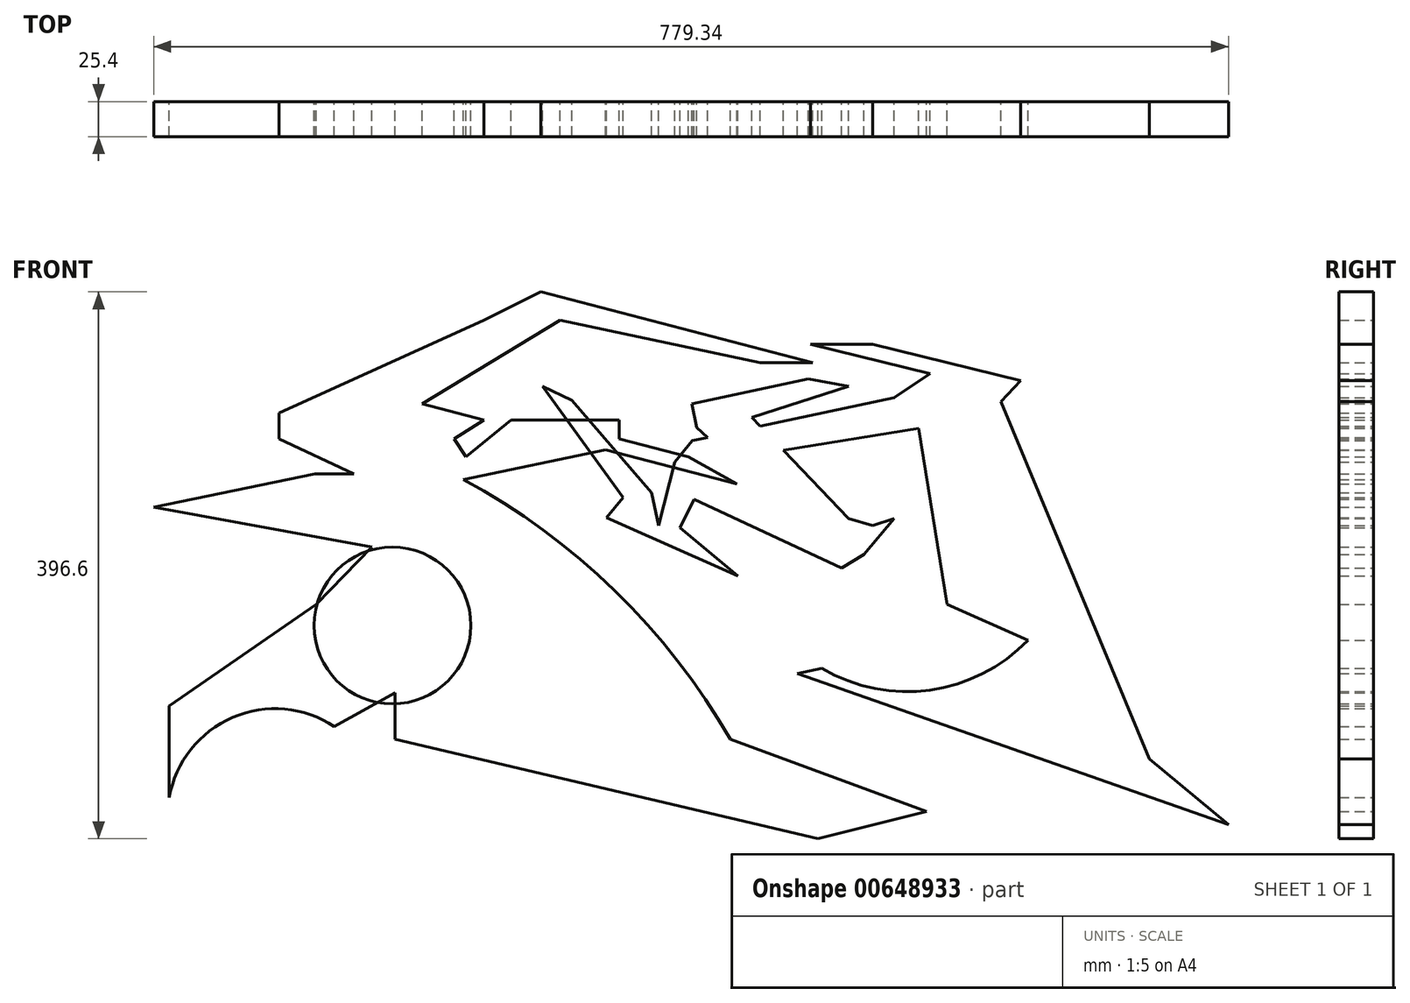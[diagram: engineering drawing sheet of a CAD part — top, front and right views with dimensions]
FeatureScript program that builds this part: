
annotation { "Feature Type Name" : "Feature", "Feature Type Description" : "" }
export const myFeature = defineFeature(function(context is Context, id is Id, definition is map)
    precondition{}
    {
        {
            var Q0;
            Q0=qCreatedBy(makeId("Front.planeOp"),FACE);
            var sketch = newSketch(context, id + "F0", { "sketchPlane" : qUnion([Q0])});
            skCircle(sketch, "E0", {"center": v(-11.54, -15.47) * mm, "radius": 56.87 * mm});
            skLineSegment(sketch, "E1", {"start": v(-55.28, -53.52) * mm, "end": v(-83.75, -13.85) * mm});
            skLineSegment(sketch, "E2", {"start": v(-83.75, -13.85) * mm, "end": v(-75.93, -41.97) * mm});
            skSolve(sketch);
        }
        {
            var Q0;
            Q0=qCreatedBy(makeId("Front.planeOp"),FACE);
            var sketch = newSketch(context, id + "F1", { "sketchPlane" : qUnion([Q0])});
            skLineSegment(sketch, "E3", {"start": v(97.36, 93.18) * mm, "end": v(97.36, 103.13) * mm});
            skLineSegment(sketch, "E4", {"start": v(97.36, 103.13) * mm, "end": v(130.3, 111.83) * mm});
            skLineSegment(sketch, "E5", {"start": v(130.3, 111.83) * mm, "end": v(314.3, 26.05) * mm});
            skLineSegment(sketch, "E6", {"start": v(314.3, 26.05) * mm, "end": v(330.46, 36) * mm});
            skLineSegment(sketch, "E7", {"start": v(330.46, 36) * mm, "end": v(352.21, 62.1) * mm});
            skLineSegment(sketch, "E8", {"start": v(352.21, 62.1) * mm, "end": v(336.67, 57.13) * mm});
            skLineSegment(sketch, "E9", {"start": v(336.67, 57.13) * mm, "end": v(319.27, 62.1) * mm});
            skLineSegment(sketch, "E10", {"start": v(319.27, 62.1) * mm, "end": v(249.03, 135.45) * mm});
            skLineSegment(sketch, "E11", {"start": v(249.03, 135.45) * mm, "end": v(319.27, 157.83) * mm});
            skLineSegment(sketch, "E12", {"start": v(319.27, 157.83) * mm, "end": v(290.06, 163.42) * mm});
            skLineSegment(sketch, "E13", {"start": v(290.06, 163.42) * mm, "end": v(205.52, 145.4) * mm});
            skLineSegment(sketch, "E14", {"start": v(205.52, 145.4) * mm, "end": v(209.2, 128.15) * mm});
            skLineSegment(sketch, "E15", {"start": v(209.2, 128.15) * mm, "end": v(300, 42.21) * mm});
            skLineSegment(sketch, "E16", {"start": v(130.3, 234.42) * mm, "end": v(115.42, 202.5) * mm});
            skLineSegment(sketch, "E17", {"start": v(115.42, 202.5) * mm, "end": v(118.58, 202.5) * mm});
            skLineSegment(sketch, "E18", {"start": v(97.36, 157.83) * mm, "end": v(118.58, 147.93) * mm});
            skLineSegment(sketch, "E19", {"start": v(118.58, 147.93) * mm, "end": v(176.52, 80.93) * mm});
            skLineSegment(sketch, "E20", {"start": v(176.52, 80.93) * mm, "end": v(181.6, 57.13) * mm});
            skLineSegment(sketch, "E21", {"start": v(181.6, 57.13) * mm, "end": v(193.17, 103.13) * mm});
            skLineSegment(sketch, "E22", {"start": v(193.17, 103.13) * mm, "end": v(206.05, 118.58) * mm});
            skLineSegment(sketch, "E23", {"start": v(206.05, 118.58) * mm, "end": v(352.21, 149.74) * mm});
            skLineSegment(sketch, "E24", {"start": v(352.21, 149.74) * mm, "end": v(378.29, 167.06) * mm});
            skLineSegment(sketch, "E25", {"start": v(378.29, 167.06) * mm, "end": v(291.68, 188.47) * mm});
            skLineSegment(sketch, "E26", {"start": v(291.68, 188.47) * mm, "end": v(336.67, 188.47) * mm});
            skLineSegment(sketch, "E27", {"start": v(336.67, 188.47) * mm, "end": v(443.94, 161.95) * mm});
            skLineSegment(sketch, "E28", {"start": v(443.94, 161.95) * mm, "end": v(429.7, 146.92) * mm});
            skLineSegment(sketch, "E29", {"start": v(429.7, 146.92) * mm, "end": v(537.48, -112.1) * mm});
            skLineSegment(sketch, "E30", {"start": v(537.48, -112.1) * mm, "end": v(594.7, -159.8) * mm});
            skLineSegment(sketch, "E31", {"start": v(594.7, -159.8) * mm, "end": v(282.12, -50.37) * mm});
            skLineSegment(sketch, "E32", {"start": v(282.12, -50.37) * mm, "end": v(300, -46.56) * mm});
            skArc(sketch, "E33", {"start": v(300, -46.56) * mm, "mid": v(378.34, -62.26) * mm, "end": v(449.56, -26.05) * mm});
            skLineSegment(sketch, "E34", {"start": v(449.56, -26.05) * mm, "end": v(390.63, 0) * mm});
            skLineSegment(sketch, "E35", {"start": v(390.63, 0) * mm, "end": v(370.05, 127.35) * mm});
            skLineSegment(sketch, "E36", {"start": v(370.05, 127.35) * mm, "end": v(220.52, 103.19) * mm});
            skLineSegment(sketch, "E37", {"start": v(220.52, 103.19) * mm, "end": v(197, 55.33) * mm});
            skLineSegment(sketch, "E38", {"start": v(197, 55.33) * mm, "end": v(238.96, 20.36) * mm});
            skLineSegment(sketch, "E39", {"start": v(238.96, 20.36) * mm, "end": v(143.69, 62.8) * mm});
            skLineSegment(sketch, "E40", {"start": v(143.69, 62.8) * mm, "end": v(155.88, 77.44) * mm});
            skLineSegment(sketch, "E41", {"start": v(155.88, 77.44) * mm, "end": v(97.36, 157.83) * mm});
            skSolve(sketch);
        }
        {
            var Q0;
            {var subQ5=sQuery(id+"F1.wireOp",EDGE,"E18");Q0=makeQuery(id+"F1.imprint","IMPRINT",FACE,{"disambiguationData":[TD([[makeQuery(id+"F1.imprint","IMPRINT",EDGE,{"derivedFrom":subQ5}),-1.0]])]});}
            var Q1;
            {var subQ5=sQuery(id+"F1.wireOp",EDGE,"E24");Q1=makeQuery(id+"F1.imprint","IMPRINT",FACE,{"disambiguationData":[TD([[makeQuery(id+"F1.imprint","IMPRINT",EDGE,{"derivedFrom":subQ5}),-1.0]])]});}
            var Q2;
            {var subQ0=sQuery(id+"F1.wireOp",EDGE,"E11");Q2=makeQuery(id+"F1.imprint","IMPRINT",FACE,{"disambiguationData":[TD([[makeQuery(id+"F1.imprint","IMPRINT",EDGE,{"derivedFrom":subQ0}),1.0]])]});}
            var Q3;
            {var subQ0=sQuery(id+"F1.wireOp",EDGE,"E6");Q3=makeQuery(id+"F1.imprint","IMPRINT",FACE,{"disambiguationData":[TD([[makeQuery(id+"F1.imprint","IMPRINT",EDGE,{"derivedFrom":subQ0}),1.0]])]});}
            var Q4;
            {var subQ0=sQuery(id+"F1.wireOp",EDGE,"E20");Q4=makeQuery(id+"F1.imprint","IMPRINT",FACE,{"disambiguationData":[TD([[makeQuery(id+"F1.imprint","IMPRINT",EDGE,{"derivedFrom":subQ0}),-1.0]])]});}
            var Q5;
            {var subQ0=sQuery(id+"F1.wireOp",EDGE,"E22");Q5=makeQuery(id+"F1.imprint","IMPRINT",FACE,{"disambiguationData":[TD([[makeQuery(id+"F1.imprint","IMPRINT",EDGE,{"derivedFrom":subQ0}),-1.0]])]});}
            var Q6;
            {var subQ0=sQuery(id+"F1.wireOp",EDGE,"E36");var subQ1=sQuery(id+"F1.wireOp",EDGE,"E10");var subQ2=makeQuery(id+"F1.imprint","INTERSECT",VERTEX,{"derivedFrom":[subQ1,subQ0]});Q6=makeQuery(id+"F1.imprint","IMPRINT",FACE,{"disambiguationData":[TD([[makeQuery(id+"F1.imprint","IMPRINT",EDGE,{"disambiguationData":[TD([[subQ2,-1.0]])],"derivedFrom":subQ1}),1.0]])]});}
            var Q7;
            Q7=makeQuery(id+"F0.imprint","IMPRINT",FACE,{"disambiguationData":[TD([[makeQuery(id+"F0.imprint","IMPRINT",EDGE,{"derivedFrom":sQuery(id+"F0.wireOp",EDGE,"E0")}),1.0]])]});
            extrude(context, id + "F2", {"entities" : qUnion([Q0, Q1, Q2, Q3, Q4, Q5, Q6, Q7]), "depth" : 25.4 * mm, "offsetDistance" : 25.4 * mm});
        }
        {
            var Q0;
            Q0=qCreatedBy(makeId("Front.planeOp"),FACE);
            var sketch = newSketch(context, id + "F3", { "sketchPlane" : qUnion([Q0])});
            skLineSegment(sketch, "E42", {"start": v(-26.55, 41.3) * mm, "end": v(-184.63, 70.3) * mm});
            skLineSegment(sketch, "E43", {"start": v(-184.63, 70.3) * mm, "end": v(-67.7, 94.61) * mm});
            skLineSegment(sketch, "E44", {"start": v(-67.7, 94.61) * mm, "end": v(-39.65, 94.61) * mm});
            skLineSegment(sketch, "E45", {"start": v(-39.65, 94.61) * mm, "end": v(-93.9, 119.87) * mm});
            skLineSegment(sketch, "E46", {"start": v(-93.9, 119.87) * mm, "end": v(-93.9, 138.57) * mm});
            skLineSegment(sketch, "E47", {"start": v(-93.9, 138.57) * mm, "end": v(54.83, 205.92) * mm});
            skLineSegment(sketch, "E48", {"start": v(54.83, 205.92) * mm, "end": v(95.98, 226.5) * mm});
            skLineSegment(sketch, "E49", {"start": v(95.98, 226.5) * mm, "end": v(293.35, 175.05) * mm});
            skLineSegment(sketch, "E50", {"start": v(293.35, 175.05) * mm, "end": v(255, 175.05) * mm});
            skLineSegment(sketch, "E51", {"start": v(255, 175.05) * mm, "end": v(110.02, 205.92) * mm});
            skLineSegment(sketch, "E52", {"start": v(110.02, 205.92) * mm, "end": v(9.93, 145.12) * mm});
            skLineSegment(sketch, "E53", {"start": v(9.93, 145.12) * mm, "end": v(54.83, 133.42) * mm});
            skLineSegment(sketch, "E54", {"start": v(54.83, 133.42) * mm, "end": v(33.31, 119.87) * mm});
            skLineSegment(sketch, "E55", {"start": v(33.31, 119.87) * mm, "end": v(41.61, 106.7) * mm});
            skLineSegment(sketch, "E56", {"start": v(41.61, 106.7) * mm, "end": v(74.47, 133.42) * mm});
            skLineSegment(sketch, "E57", {"start": v(74.47, 133.42) * mm, "end": v(153.04, 133.42) * mm});
            skLineSegment(sketch, "E58", {"start": v(153.04, 133.42) * mm, "end": v(153.04, 119.87) * mm});
            skLineSegment(sketch, "E59", {"start": v(153.04, 119.87) * mm, "end": v(203.08, 106.82) * mm});
            skLineSegment(sketch, "E60", {"start": v(203.08, 106.82) * mm, "end": v(238.16, 87.13) * mm});
            skLineSegment(sketch, "E61", {"start": v(238.16, 87.13) * mm, "end": v(143.12, 111.9) * mm});
            skLineSegment(sketch, "E62", {"start": v(143.12, 111.9) * mm, "end": v(39.91, 90.44) * mm});
            skArc(sketch, "E63", {"start": v(233.49, -98.08) * mm, "mid": v(149.8, 9.64) * mm, "end": v(39.91, 90.44) * mm});
            skLineSegment(sketch, "E64", {"start": v(233.49, -98.08) * mm, "end": v(375.66, -150.46) * mm});
            skLineSegment(sketch, "E65", {"start": v(375.66, -150.46) * mm, "end": v(297.1, -170.1) * mm});
            skLineSegment(sketch, "E66", {"start": v(297.1, -170.1) * mm, "end": v(-9.71, -98.08) * mm});
            skLineSegment(sketch, "E67", {"start": v(-9.71, -98.08) * mm, "end": v(-9.71, -64.4) * mm});
            skLineSegment(sketch, "E68", {"start": v(-9.71, -64.4) * mm, "end": v(-53.68, -88.72) * mm});
            skArc(sketch, "E69", {"start": v(-53.68, -88.72) * mm, "mid": v(-127.42, -82.13) * mm, "end": v(-173.4, -140.17) * mm});
            skLineSegment(sketch, "E70", {"start": v(-173.4, -140.17) * mm, "end": v(-173.4, -73.76) * mm});
            skLineSegment(sketch, "E71", {"start": v(-173.4, -73.76) * mm, "end": v(-66.77, 0) * mm});
            skLineSegment(sketch, "E72", {"start": v(-66.77, 0) * mm, "end": v(-26.55, 41.3) * mm});
            skSolve(sketch);
        }
        {
            var Q0;
            Q0 = qSketchRegion(id + "F3", true);
            extrude(context, id + "F4", {"entities" : qUnion([Q0]), "depth" : 25.4 * mm, "offsetDistance" : 25.4 * mm});
        }
    });
